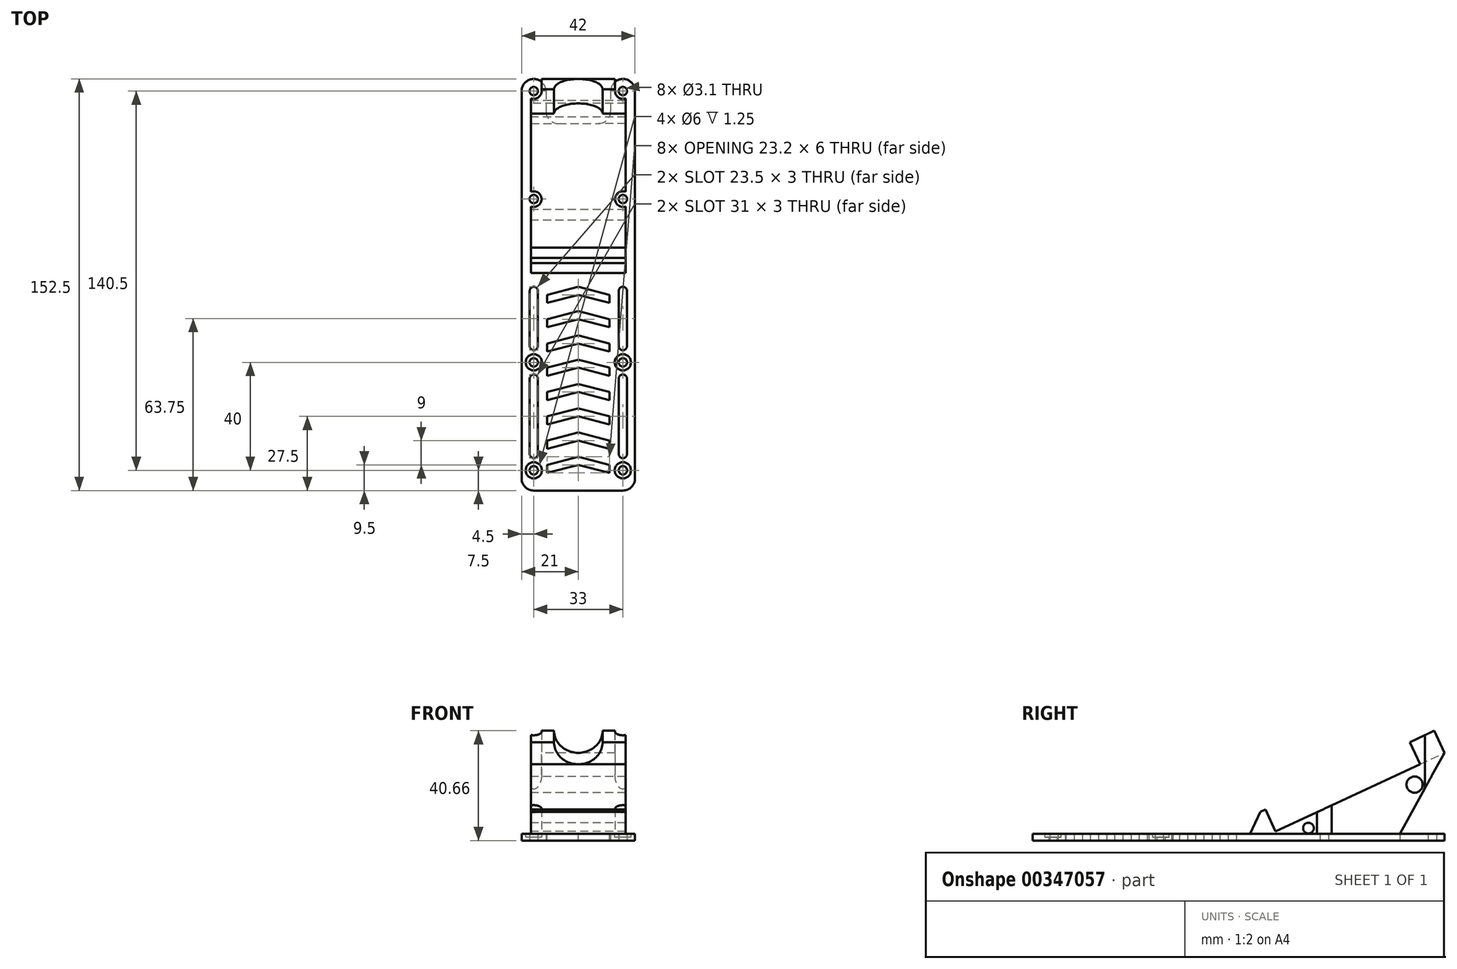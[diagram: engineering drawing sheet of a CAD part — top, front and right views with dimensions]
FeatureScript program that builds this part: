
annotation { "Feature Type Name" : "Feature", "Feature Type Description" : "" }
export const myFeature = defineFeature(function(context is Context, id is Id, definition is map)
    precondition{}
    {
        {
            var Q0;
            Q0=qCreatedBy(makeId("Top.planeOp"),FACE);
            var sketch = newSketch(context, id + "F0", { "sketchPlane" : qUnion([Q0])});
            skLineSegment(sketch, "E0.bottom", {"start": v(-16.5, 76.75) * mm, "end": v(-16.5, 76.75) * mm});
            skCircle(sketch, "E1", {"center": v(16.5, 72.25) * mm, "radius": 1.55 * mm});
            skPoint(sketch, "E2.visualSharp", {"position": v(21, 76.75) * mm});
            skArc(sketch, "E2.filletArc", {"start": v(21, 72.25) * mm, "mid": v(19.68, 75.43) * mm, "end": v(16.5, 76.75) * mm});
            skCircle(sketch, "E3", {"center": v(-16.5, 72.25) * mm, "radius": 1.55 * mm});
            skLineSegment(sketch, "E4", {"start": v(-12, 72.25) * mm, "end": v(-12, 64.75) * mm});
            skLineSegment(sketch, "E5", {"start": v(12, 72.25) * mm, "end": v(12, 64.75) * mm});
            skLineSegment(sketch, "E6", {"start": v(-7.5, 60.25) * mm, "end": v(7.5, 60.25) * mm});
            skLineSegment(sketch, "E7.trimOffspring", {"start": v(16.5, 76.75) * mm, "end": v(16.5, 76.75) * mm});
            skPoint(sketch, "E8.visualSharp", {"position": v(-12, 76.75) * mm});
            skArc(sketch, "E8.filletArc", {"start": v(-12, 72.25) * mm, "mid": v(-13.32, 75.43) * mm, "end": v(-16.5, 76.75) * mm});
            skPoint(sketch, "E9.visualSharp", {"position": v(-21, 76.75) * mm});
            skArc(sketch, "E9.filletArc", {"start": v(-16.5, 76.75) * mm, "mid": v(-19.68, 75.43) * mm, "end": v(-21, 72.25) * mm});
            skPoint(sketch, "E10.visualSharp", {"position": v(12, 76.75) * mm});
            skArc(sketch, "E10.filletArc", {"start": v(16.5, 76.75) * mm, "mid": v(13.32, 75.43) * mm, "end": v(12, 72.25) * mm});
            skArc(sketch, "E11.filletArc", {"start": v(7.5, 60.25) * mm, "mid": v(10.68, 61.57) * mm, "end": v(12, 64.75) * mm});
            skArc(sketch, "E12.filletArc", {"start": v(-12, 64.75) * mm, "mid": v(-10.68, 61.57) * mm, "end": v(-7.5, 60.25) * mm});
            skLineSegment(sketch, "E13", {"start": v(-16.5, -0.25) * mm, "end": v(-16.5, -0.25) * mm});
            skLineSegment(sketch, "E14", {"start": v(-16.5, -23.75) * mm, "end": v(-16.5, -23.75) * mm});
            skLineSegment(sketch, "E15", {"start": v(16.5, -23.75) * mm, "end": v(16.5, -23.75) * mm});
            skLineSegment(sketch, "E16", {"start": v(16.5, -0.25) * mm, "end": v(16.5, -0.25) * mm});
            skLineSegment(sketch, "E17.trimOffspring", {"start": v(15, -1.75) * mm, "end": v(15, -22.25) * mm});
            skLineSegment(sketch, "E18.trimOffspring", {"start": v(-15, -1.75) * mm, "end": v(-15, -22.25) * mm});
            skCircle(sketch, "E19", {"center": v(16.5, 32.25) * mm, "radius": 1.55 * mm});
            skCircle(sketch, "E20", {"center": v(-16.5, 32.25) * mm, "radius": 1.55 * mm});
            skPoint(sketch, "E21.visualSharp", {"position": v(18, -0.25) * mm});
            skPoint(sketch, "E22.visualSharp", {"position": v(15, -0.25) * mm});
            skArc(sketch, "E22.filletArc", {"start": v(16.5, -0.25) * mm, "mid": v(15.44, -0.69) * mm, "end": v(15, -1.75) * mm});
            skPoint(sketch, "E23.visualSharp", {"position": v(-15, -0.25) * mm});
            skArc(sketch, "E23.filletArc", {"start": v(-15, -1.75) * mm, "mid": v(-15.44, -0.69) * mm, "end": v(-16.5, -0.25) * mm});
            skPoint(sketch, "E24.visualSharp", {"position": v(-18, -0.25) * mm});
            skCircle(sketch, "E25", {"center": v(16.5, -28.25) * mm, "radius": 1.55 * mm});
            skPoint(sketch, "E25.centerSnap0", {"position": v(16.5, -23.75) * mm});
            skCircle(sketch, "E26", {"center": v(-16.5, -28.25) * mm, "radius": 1.55 * mm});
            skPoint(sketch, "E26.centerSnap0", {"position": v(-16.5, -23.75) * mm});
            skPoint(sketch, "E27.visualSharp", {"position": v(18, -23.75) * mm});
            skPoint(sketch, "E28.visualSharp", {"position": v(-15, -23.75) * mm});
            skArc(sketch, "E28.filletArc", {"start": v(-16.5, -23.75) * mm, "mid": v(-15.44, -23.31) * mm, "end": v(-15, -22.25) * mm});
            skPoint(sketch, "E29.visualSharp", {"position": v(-18, -23.75) * mm});
            skPoint(sketch, "E30.visualSharp", {"position": v(15, -23.75) * mm});
            skArc(sketch, "E30.filletArc", {"start": v(15, -22.25) * mm, "mid": v(15.44, -23.31) * mm, "end": v(16.5, -23.75) * mm});
            skPoint(sketch, "E31", {"position": v(-16.5, -68.25) * mm});
            skPoint(sketch, "E32", {"position": v(16.5, -68.25) * mm});
            skLineSegment(sketch, "E33", {"start": v(-16.5, -75.75) * mm, "end": v(16.5, -75.75) * mm});
            skLineSegment(sketch, "E34", {"start": v(-21, 72.25) * mm, "end": v(-21, -71.25) * mm});
            skLineSegment(sketch, "E35", {"start": v(21, 72.25) * mm, "end": v(21, -71.25) * mm});
            skCircle(sketch, "E36", {"center": v(-16.5, -68.25) * mm, "radius": 1.55 * mm});
            skCircle(sketch, "E37", {"center": v(16.5, -68.25) * mm, "radius": 1.55 * mm});
            skPoint(sketch, "E38.visualSharp", {"position": v(-21, -75.75) * mm});
            skArc(sketch, "E38.filletArc", {"start": v(-21, -71.25) * mm, "mid": v(-19.68, -74.43) * mm, "end": v(-16.5, -75.75) * mm});
            skPoint(sketch, "E39.visualSharp", {"position": v(21, -75.75) * mm});
            skArc(sketch, "E39.filletArc", {"start": v(16.5, -75.75) * mm, "mid": v(19.68, -74.43) * mm, "end": v(21, -71.25) * mm});
            skLineSegment(sketch, "E40", {"start": v(-15, -34.25) * mm, "end": v(-15, -62.25) * mm});
            skLineSegment(sketch, "E41", {"start": v(-16.5, -63.75) * mm, "end": v(-16.5, -63.75) * mm});
            skLineSegment(sketch, "E42", {"start": v(-16.5, -32.75) * mm, "end": v(-16.5, -32.75) * mm});
            skLineSegment(sketch, "E43", {"start": v(15, -34.25) * mm, "end": v(15, -62.25) * mm});
            skLineSegment(sketch, "E44", {"start": v(16.5, -63.75) * mm, "end": v(16.5, -63.75) * mm});
            skLineSegment(sketch, "E45", {"start": v(16.5, -32.75) * mm, "end": v(16.5, -32.75) * mm});
            skPoint(sketch, "E46.visualSharp", {"position": v(-15, -32.75) * mm});
            skArc(sketch, "E46.filletArc", {"start": v(-15, -34.25) * mm, "mid": v(-15.44, -33.19) * mm, "end": v(-16.5, -32.75) * mm});
            skPoint(sketch, "E47.visualSharp", {"position": v(15, -32.75) * mm});
            skArc(sketch, "E47.filletArc", {"start": v(16.5, -32.75) * mm, "mid": v(15.44, -33.19) * mm, "end": v(15, -34.25) * mm});
            skPoint(sketch, "E48.visualSharp", {"position": v(-15, -63.75) * mm});
            skArc(sketch, "E48.filletArc", {"start": v(-16.5, -63.75) * mm, "mid": v(-15.44, -63.31) * mm, "end": v(-15, -62.25) * mm});
            skPoint(sketch, "E49.visualSharp", {"position": v(15, -63.75) * mm});
            skArc(sketch, "E49.filletArc", {"start": v(15, -62.25) * mm, "mid": v(15.44, -63.31) * mm, "end": v(16.5, -63.75) * mm});
            skLineSegment(sketch, "E50", {"start": v(18, -1.75) * mm, "end": v(18, -22.25) * mm});
            skLineSegment(sketch, "E51", {"start": v(18, -34.25) * mm, "end": v(18, -62.25) * mm});
            skArc(sketch, "E52.filletArc", {"start": v(18, -1.75) * mm, "mid": v(17.56, -0.69) * mm, "end": v(16.5, -0.25) * mm});
            skArc(sketch, "E53.filletArc", {"start": v(16.5, -23.75) * mm, "mid": v(17.56, -23.31) * mm, "end": v(18, -22.25) * mm});
            skPoint(sketch, "E54.visualSharp", {"position": v(18, -32.75) * mm});
            skArc(sketch, "E54.filletArc", {"start": v(18, -34.25) * mm, "mid": v(17.56, -33.19) * mm, "end": v(16.5, -32.75) * mm});
            skPoint(sketch, "E55.visualSharp", {"position": v(18, -63.75) * mm});
            skArc(sketch, "E55.filletArc", {"start": v(16.5, -63.75) * mm, "mid": v(17.56, -63.31) * mm, "end": v(18, -62.25) * mm});
            skLineSegment(sketch, "E56", {"start": v(-18, -1.75) * mm, "end": v(-18, -22.25) * mm});
            skLineSegment(sketch, "E57", {"start": v(-18, -34.25) * mm, "end": v(-18, -62.25) * mm});
            skPoint(sketch, "E58.orphan", {"position": v(-21, -63.75) * mm});
            skArc(sketch, "E59.filletArc", {"start": v(-16.5, -0.25) * mm, "mid": v(-17.56, -0.69) * mm, "end": v(-18, -1.75) * mm});
            skArc(sketch, "E60.filletArc", {"start": v(-18, -22.25) * mm, "mid": v(-17.56, -23.31) * mm, "end": v(-16.5, -23.75) * mm});
            skPoint(sketch, "E61.visualSharp", {"position": v(-18, -32.75) * mm});
            skArc(sketch, "E61.filletArc", {"start": v(-16.5, -32.75) * mm, "mid": v(-17.56, -33.19) * mm, "end": v(-18, -34.25) * mm});
            skPoint(sketch, "E62.visualSharp", {"position": v(-18, -63.75) * mm});
            skArc(sketch, "E62.filletArc", {"start": v(-18, -62.25) * mm, "mid": v(-17.56, -63.31) * mm, "end": v(-16.5, -63.75) * mm});
            skSolve(sketch);
        }
        {
            var Q0;
            Q0=qCreatedBy(makeId("Right.planeOp"),FACE);
            var sketch = newSketch(context, id + "F1", { "sketchPlane" : qUnion([Q0])});
            skLineSegment(sketch, "E63", {"start": v(12.4, 2.5) * mm, "end": v(76.75, 32.5) * mm});
            skLineSegment(sketch, "E64", {"start": v(76.75, 32.5) * mm, "end": v(72.95, 40.66) * mm});
            skLineSegment(sketch, "E65", {"start": v(72.95, 40.66) * mm, "end": v(63.88, 36.44) * mm});
            skLineSegment(sketch, "E66", {"start": v(63.88, 36.44) * mm, "end": v(67.69, 28.28) * mm});
            skLineSegment(sketch, "E67", {"start": v(12.4, 2.5) * mm, "end": v(8.6, 10.66) * mm});
            skLineSegment(sketch, "E68", {"start": v(8.6, 10.66) * mm, "end": v(10.41, 11.5) * mm});
            skLineSegment(sketch, "E69", {"start": v(10.41, 11.5) * mm, "end": v(14.21, 3.35) * mm});
            skPoint(sketch, "E70.0", {"position": v(60.25, 0) * mm});
            skLineSegment(sketch, "E71", {"start": v(76.74, 0) * mm, "end": v(76.74, 2.5) * mm});
            skLineSegment(sketch, "E72", {"start": v(-5.7, 2.5) * mm, "end": v(-5.7, 0) * mm});
            skLineSegment(sketch, "E73", {"start": v(-5.7, 0) * mm, "end": v(76.74, 0) * mm});
            skLineSegment(sketch, "E74", {"start": v(-5.7, 2.5) * mm, "end": v(76.74, 2.5) * mm});
            skLineSegment(sketch, "E75", {"start": v(76.75, 32.5) * mm, "end": v(60.25, 2.5) * mm});
            skLineSegment(sketch, "E76", {"start": v(8.6, 10.66) * mm, "end": v(8.6, 2.5) * mm});
            skLineSegment(sketch, "E77", {"start": v(60.25, 2.5) * mm, "end": v(60.25, 24.81) * mm, "construction": true});
            skPoint(sketch, "E78", {"position": v(63.16, 26.17) * mm});
            skLineSegment(sketch, "E79", {"start": v(63.16, 26.17) * mm, "end": v(67.8, 16.22) * mm, "construction": true});
            skCircle(sketch, "E80", {"center": v(65.7, 20.73) * mm, "radius": 3 * mm});
            skLineSegment(sketch, "E81", {"start": v(8.6, 10.66) * mm, "end": v(4.8, 2.5) * mm});
            skCircle(sketch, "E82", {"center": v(26.37, 4.6) * mm, "radius": 2 * mm});
            skSolve(sketch);
        }
        {
            var Q0;
            {var subQ0=sQuery(id+"F1.wireOp",EDGE,"E67");Q0=makeQuery(id+"F1.imprint","IMPRINT",FACE,{"disambiguationData":[TD([[makeQuery(id+"F1.imprint","IMPRINT",EDGE,{"derivedFrom":subQ0}),-1.0]])]});}
            var Q1;
            {var subQ0=sQuery(id+"F1.wireOp",EDGE,"E64");Q1=makeQuery(id+"F1.imprint","IMPRINT",FACE,{"disambiguationData":[TD([[makeQuery(id+"F1.imprint","IMPRINT",EDGE,{"derivedFrom":subQ0}),1.0]])]});}
            var Q2;
            {var subQ4=sQuery(id+"F1.wireOp",EDGE,"E75");Q2=makeQuery(id+"F1.imprint","IMPRINT",FACE,{"disambiguationData":[TD([[makeQuery(id+"F1.imprint","IMPRINT",EDGE,{"derivedFrom":subQ4}),-1.0]])]});}
            var Q3;
            {var subQ0=sQuery(id+"F1.wireOp",EDGE,"E67");Q3=makeQuery(id+"F1.imprint","IMPRINT",FACE,{"disambiguationData":[TD([[makeQuery(id+"F1.imprint","IMPRINT",EDGE,{"derivedFrom":subQ0}),1.0]])]});}
            var Q4;
            {var subQ0=sQuery(id+"F1.wireOp",EDGE,"E76");Q4=makeQuery(id+"F1.imprint","IMPRINT",FACE,{"disambiguationData":[TD([[makeQuery(id+"F1.imprint","IMPRINT",EDGE,{"derivedFrom":subQ0}),-1.0]])]});}
            extrude(context, id + "F2", {"entities" : qUnion([Q0, Q1, Q2, Q3, Q4]), "depth" : 17.5 * mm, "hasSecondDirection" : true, "secondDirectionOppositeDirection" : true, "secondDirectionDepth" : 17.5 * mm});
        }
        {
            var Q0;
            Q0=makeQuery(id+"F2.opExtrude","SWEPT_FACE",FACE,{"disambiguationData":[OSD([sQuery(id+"F1.wireOp",EDGE,"E64")])]});
            var sketch = newSketch(context, id + "F3", { "sketchPlane" : qUnion([Q0])});
            skLineSegment(sketch, "E83.0", {"start": v(-17.5, -2.98) * mm, "end": v(17.5, -2.98) * mm, "construction": true});
            skLineSegment(sketch, "E84", {"start": v(0, -2.98) * mm, "end": v(0, 15.02) * mm, "construction": true});
            skPoint(sketch, "E84.endSnap0", {"position": v(0, -2.98) * mm});
            skCircle(sketch, "E85", {"center": v(0, 6.02) * mm, "radius": 9 * mm});
            skSolve(sketch);
        }
        {
            var Q0;
            Q0 = qSketchRegion(id + "F3", true);
            extrude(context, id + "F4", {"entities" : qUnion([Q0]), "operationType" : NewBodyOperationType.REMOVE, "oppositeDirection" : true, "depth" : 25 * mm});
        }
        {
            var Q0;
            Q0=makeQuery(id+"F0.imprint","IMPRINT",FACE,{"disambiguationData":[TD([[makeQuery(id+"F0.imprint","IMPRINT",EDGE,{"derivedFrom":sQuery(id+"F0.wireOp",EDGE,"E1")}),-1.0]])]});
            extrude(context, id + "F5", {"entities" : qUnion([Q0]), "operationType" : NewBodyOperationType.ADD, "depth" : 2.5 * mm});
        }
        {
            var Q0;
            Q0=makeQuery(id+"F5.opExtrude","CAP_FACE",FACE,{"disambiguationData":[OSD([sQuery(id+"F0.wireOp",EDGE,"E1"),sQuery(id+"F0.wireOp",EDGE,"E2.filletArc"),sQuery(id+"F0.wireOp",EDGE,"E3"),sQuery(id+"F0.wireOp",EDGE,"E4"),sQuery(id+"F0.wireOp",EDGE,"E5"),sQuery(id+"F0.wireOp",EDGE,"E6"),sQuery(id+"F0.wireOp",EDGE,"E8.filletArc"),sQuery(id+"F0.wireOp",EDGE,"E9.filletArc"),sQuery(id+"F0.wireOp",EDGE,"E10.filletArc"),sQuery(id+"F0.wireOp",EDGE,"E11.filletArc"),sQuery(id+"F0.wireOp",EDGE,"E12.filletArc"),sQuery(id+"F0.wireOp",EDGE,"E17.trimOffspring"),sQuery(id+"F0.wireOp",EDGE,"E18.trimOffspring"),sQuery(id+"F0.wireOp",EDGE,"E19"),sQuery(id+"F0.wireOp",EDGE,"E20"),sQuery(id+"F0.wireOp",EDGE,"E22.filletArc"),sQuery(id+"F0.wireOp",EDGE,"E23.filletArc"),sQuery(id+"F0.wireOp",EDGE,"E25"),sQuery(id+"F0.wireOp",EDGE,"E26"),sQuery(id+"F0.wireOp",EDGE,"E28.filletArc"),sQuery(id+"F0.wireOp",EDGE,"E30.filletArc"),sQuery(id+"F0.wireOp",EDGE,"E33"),sQuery(id+"F0.wireOp",EDGE,"E34"),sQuery(id+"F0.wireOp",EDGE,"E35"),sQuery(id+"F0.wireOp",EDGE,"E36"),sQuery(id+"F0.wireOp",EDGE,"E37"),sQuery(id+"F0.wireOp",EDGE,"E38.filletArc"),sQuery(id+"F0.wireOp",EDGE,"E39.filletArc"),sQuery(id+"F0.wireOp",EDGE,"E13"),sQuery(id+"F0.wireOp",EDGE,"E14"),sQuery(id+"F0.wireOp",EDGE,"E16"),sQuery(id+"F0.wireOp",EDGE,"E15")])],"isStart":false});
            var sketch = newSketch(context, id + "F6", { "sketchPlane" : qUnion([Q0])});
            skCircle(sketch, "E86", {"center": v(16.5, 72.25) * mm, "radius": 2.9 * mm});
            skCircle(sketch, "E87", {"center": v(-16.5, 72.25) * mm, "radius": 2.9 * mm});
            skCircle(sketch, "E88", {"center": v(-16.5, 32.25) * mm, "radius": 2.9 * mm});
            skCircle(sketch, "E89", {"center": v(16.5, 32.25) * mm, "radius": 2.9 * mm});
            skCircle(sketch, "E90", {"center": v(-16.5, -28.25) * mm, "radius": 3 * mm});
            skCircle(sketch, "E91", {"center": v(16.5, -28.25) * mm, "radius": 3 * mm});
            skCircle(sketch, "E92", {"center": v(-16.5, -68.25) * mm, "radius": 3 * mm});
            skCircle(sketch, "E93", {"center": v(16.5, -68.25) * mm, "radius": 3 * mm});
            skSolve(sketch);
        }
        {
            var Q0;
            Q0=makeQuery(id+"F6.imprint","IMPRINT",FACE,{"disambiguationData":[TD([[makeQuery(id+"F6.imprint","IMPRINT",EDGE,{"derivedFrom":makeQuery(id+"F5.opExtrude","CAP_EDGE",EDGE,{"disambiguationData":[OSD([sQuery(id+"F0.wireOp",EDGE,"E25")])],"isStart":false})}),1.0]])]});
            var Q1;
            Q1=makeQuery(id+"F6.imprint","IMPRINT",FACE,{"disambiguationData":[TD([[makeQuery(id+"F6.imprint","IMPRINT",EDGE,{"derivedFrom":makeQuery(id+"F5.opExtrude","CAP_EDGE",EDGE,{"disambiguationData":[OSD([sQuery(id+"F0.wireOp",EDGE,"E26")])],"isStart":false})}),1.0]])]});
            var Q2;
            Q2=makeQuery(id+"F6.imprint","IMPRINT",FACE,{"disambiguationData":[TD([[makeQuery(id+"F6.imprint","IMPRINT",EDGE,{"derivedFrom":makeQuery(id+"F5.opExtrude","CAP_EDGE",EDGE,{"disambiguationData":[OSD([sQuery(id+"F0.wireOp",EDGE,"E36")])],"isStart":false})}),1.0]])]});
            var Q3;
            Q3=makeQuery(id+"F6.imprint","IMPRINT",FACE,{"disambiguationData":[TD([[makeQuery(id+"F6.imprint","IMPRINT",EDGE,{"derivedFrom":makeQuery(id+"F5.opExtrude","CAP_EDGE",EDGE,{"disambiguationData":[OSD([sQuery(id+"F0.wireOp",EDGE,"E37")])],"isStart":false})}),1.0]])]});
            var Q4;
            Q4=makeQuery(id+"F6.imprint","IMPRINT",FACE,{"disambiguationData":[TD([[makeQuery(id+"F6.imprint","IMPRINT",EDGE,{"derivedFrom":sQuery(id+"F6.wireOp",EDGE,"E90")}),1.0]])]});
            var Q5;
            Q5=makeQuery(id+"F6.imprint","IMPRINT",FACE,{"disambiguationData":[TD([[makeQuery(id+"F6.imprint","IMPRINT",EDGE,{"derivedFrom":sQuery(id+"F6.wireOp",EDGE,"E91")}),1.0]])]});
            var Q6;
            Q6=makeQuery(id+"F6.imprint","IMPRINT",FACE,{"disambiguationData":[TD([[makeQuery(id+"F6.imprint","IMPRINT",EDGE,{"derivedFrom":sQuery(id+"F6.wireOp",EDGE,"E92")}),1.0]])]});
            var Q7;
            Q7=makeQuery(id+"F6.imprint","IMPRINT",FACE,{"disambiguationData":[TD([[makeQuery(id+"F6.imprint","IMPRINT",EDGE,{"derivedFrom":sQuery(id+"F6.wireOp",EDGE,"E93")}),1.0]])]});
            var Q8;
            {var subQ9=sQuery(id+"F0.wireOp",EDGE,"E20");var subQ10=makeQuery(id+"F5.opExtrude","CAP_FACE",FACE,{"disambiguationData":[OSD([sQuery(id+"F0.wireOp",EDGE,"E1"),sQuery(id+"F0.wireOp",EDGE,"E2.filletArc"),sQuery(id+"F0.wireOp",EDGE,"E3"),sQuery(id+"F0.wireOp",EDGE,"E4"),sQuery(id+"F0.wireOp",EDGE,"E5"),sQuery(id+"F0.wireOp",EDGE,"E6"),sQuery(id+"F0.wireOp",EDGE,"E8.filletArc"),sQuery(id+"F0.wireOp",EDGE,"E9.filletArc"),sQuery(id+"F0.wireOp",EDGE,"E10.filletArc"),sQuery(id+"F0.wireOp",EDGE,"E11.filletArc"),sQuery(id+"F0.wireOp",EDGE,"E12.filletArc"),sQuery(id+"F0.wireOp",EDGE,"E17.trimOffspring"),sQuery(id+"F0.wireOp",EDGE,"E18.trimOffspring"),sQuery(id+"F0.wireOp",EDGE,"E19"),subQ9,sQuery(id+"F0.wireOp",EDGE,"E22.filletArc"),sQuery(id+"F0.wireOp",EDGE,"E23.filletArc"),sQuery(id+"F0.wireOp",EDGE,"E25"),sQuery(id+"F0.wireOp",EDGE,"E26"),sQuery(id+"F0.wireOp",EDGE,"E28.filletArc"),sQuery(id+"F0.wireOp",EDGE,"E30.filletArc"),sQuery(id+"F0.wireOp",EDGE,"E33"),sQuery(id+"F0.wireOp",EDGE,"E34"),sQuery(id+"F0.wireOp",EDGE,"E35"),sQuery(id+"F0.wireOp",EDGE,"E36"),sQuery(id+"F0.wireOp",EDGE,"E37"),sQuery(id+"F0.wireOp",EDGE,"E38.filletArc"),sQuery(id+"F0.wireOp",EDGE,"E39.filletArc"),sQuery(id+"F0.wireOp",EDGE,"E13"),sQuery(id+"F0.wireOp",EDGE,"E14"),sQuery(id+"F0.wireOp",EDGE,"E16"),sQuery(id+"F0.wireOp",EDGE,"E15"),sQuery(id+"F0.wireOp",EDGE,"E40"),sQuery(id+"F0.wireOp",EDGE,"E41"),sQuery(id+"F0.wireOp",EDGE,"E42"),sQuery(id+"F0.wireOp",EDGE,"E43"),sQuery(id+"F0.wireOp",EDGE,"E44"),sQuery(id+"F0.wireOp",EDGE,"E45"),sQuery(id+"F0.wireOp",EDGE,"E46.filletArc"),sQuery(id+"F0.wireOp",EDGE,"E47.filletArc"),sQuery(id+"F0.wireOp",EDGE,"E48.filletArc"),sQuery(id+"F0.wireOp",EDGE,"E49.filletArc")])],"isStart":false});var subQ17=makeQuery(id+"F5.boolean.opBoolean","SPLIT",EDGE,{"disambiguationData":[topologyDisambiguationEdgeConnected([subQ10])],"derivedFrom":makeQuery(id+"F5.opExtrude","CAP_EDGE",EDGE,{"disambiguationData":[OSD([subQ9])],"isStart":false})});Q8=makeQuery(id+"F6.imprint","IMPRINT",FACE,{"disambiguationData":[TD([[makeQuery(id+"F6.imprint","IMPRINT",EDGE,{"derivedFrom":subQ17}),1.0]])]});}
            var Q9;
            {var subQ9=sQuery(id+"F0.wireOp",EDGE,"E19");var subQ10=makeQuery(id+"F5.opExtrude","CAP_FACE",FACE,{"disambiguationData":[OSD([sQuery(id+"F0.wireOp",EDGE,"E1"),sQuery(id+"F0.wireOp",EDGE,"E2.filletArc"),sQuery(id+"F0.wireOp",EDGE,"E3"),sQuery(id+"F0.wireOp",EDGE,"E4"),sQuery(id+"F0.wireOp",EDGE,"E5"),sQuery(id+"F0.wireOp",EDGE,"E6"),sQuery(id+"F0.wireOp",EDGE,"E8.filletArc"),sQuery(id+"F0.wireOp",EDGE,"E9.filletArc"),sQuery(id+"F0.wireOp",EDGE,"E10.filletArc"),sQuery(id+"F0.wireOp",EDGE,"E11.filletArc"),sQuery(id+"F0.wireOp",EDGE,"E12.filletArc"),sQuery(id+"F0.wireOp",EDGE,"E17.trimOffspring"),sQuery(id+"F0.wireOp",EDGE,"E18.trimOffspring"),subQ9,sQuery(id+"F0.wireOp",EDGE,"E20"),sQuery(id+"F0.wireOp",EDGE,"E22.filletArc"),sQuery(id+"F0.wireOp",EDGE,"E23.filletArc"),sQuery(id+"F0.wireOp",EDGE,"E25"),sQuery(id+"F0.wireOp",EDGE,"E26"),sQuery(id+"F0.wireOp",EDGE,"E28.filletArc"),sQuery(id+"F0.wireOp",EDGE,"E30.filletArc"),sQuery(id+"F0.wireOp",EDGE,"E33"),sQuery(id+"F0.wireOp",EDGE,"E34"),sQuery(id+"F0.wireOp",EDGE,"E35"),sQuery(id+"F0.wireOp",EDGE,"E36"),sQuery(id+"F0.wireOp",EDGE,"E37"),sQuery(id+"F0.wireOp",EDGE,"E38.filletArc"),sQuery(id+"F0.wireOp",EDGE,"E39.filletArc"),sQuery(id+"F0.wireOp",EDGE,"E13"),sQuery(id+"F0.wireOp",EDGE,"E14"),sQuery(id+"F0.wireOp",EDGE,"E16"),sQuery(id+"F0.wireOp",EDGE,"E15"),sQuery(id+"F0.wireOp",EDGE,"E40"),sQuery(id+"F0.wireOp",EDGE,"E41"),sQuery(id+"F0.wireOp",EDGE,"E42"),sQuery(id+"F0.wireOp",EDGE,"E43"),sQuery(id+"F0.wireOp",EDGE,"E44"),sQuery(id+"F0.wireOp",EDGE,"E45"),sQuery(id+"F0.wireOp",EDGE,"E46.filletArc"),sQuery(id+"F0.wireOp",EDGE,"E47.filletArc"),sQuery(id+"F0.wireOp",EDGE,"E48.filletArc"),sQuery(id+"F0.wireOp",EDGE,"E49.filletArc")])],"isStart":false});var subQ17=makeQuery(id+"F5.boolean.opBoolean","SPLIT",EDGE,{"disambiguationData":[topologyDisambiguationEdgeConnected([subQ10])],"derivedFrom":makeQuery(id+"F5.opExtrude","CAP_EDGE",EDGE,{"disambiguationData":[OSD([subQ9])],"isStart":false})});Q9=makeQuery(id+"F6.imprint","IMPRINT",FACE,{"disambiguationData":[TD([[makeQuery(id+"F6.imprint","IMPRINT",EDGE,{"derivedFrom":subQ17}),1.0]])]});}
            var Q10;
            {var subQ9=sQuery(id+"F0.wireOp",EDGE,"E20");var subQ10=makeQuery(id+"F5.opExtrude","CAP_FACE",FACE,{"disambiguationData":[OSD([sQuery(id+"F0.wireOp",EDGE,"E1"),sQuery(id+"F0.wireOp",EDGE,"E2.filletArc"),sQuery(id+"F0.wireOp",EDGE,"E3"),sQuery(id+"F0.wireOp",EDGE,"E4"),sQuery(id+"F0.wireOp",EDGE,"E5"),sQuery(id+"F0.wireOp",EDGE,"E6"),sQuery(id+"F0.wireOp",EDGE,"E8.filletArc"),sQuery(id+"F0.wireOp",EDGE,"E9.filletArc"),sQuery(id+"F0.wireOp",EDGE,"E10.filletArc"),sQuery(id+"F0.wireOp",EDGE,"E11.filletArc"),sQuery(id+"F0.wireOp",EDGE,"E12.filletArc"),sQuery(id+"F0.wireOp",EDGE,"E17.trimOffspring"),sQuery(id+"F0.wireOp",EDGE,"E18.trimOffspring"),sQuery(id+"F0.wireOp",EDGE,"E19"),subQ9,sQuery(id+"F0.wireOp",EDGE,"E22.filletArc"),sQuery(id+"F0.wireOp",EDGE,"E23.filletArc"),sQuery(id+"F0.wireOp",EDGE,"E25"),sQuery(id+"F0.wireOp",EDGE,"E26"),sQuery(id+"F0.wireOp",EDGE,"E28.filletArc"),sQuery(id+"F0.wireOp",EDGE,"E30.filletArc"),sQuery(id+"F0.wireOp",EDGE,"E33"),sQuery(id+"F0.wireOp",EDGE,"E34"),sQuery(id+"F0.wireOp",EDGE,"E35"),sQuery(id+"F0.wireOp",EDGE,"E36"),sQuery(id+"F0.wireOp",EDGE,"E37"),sQuery(id+"F0.wireOp",EDGE,"E38.filletArc"),sQuery(id+"F0.wireOp",EDGE,"E39.filletArc"),sQuery(id+"F0.wireOp",EDGE,"E13"),sQuery(id+"F0.wireOp",EDGE,"E14"),sQuery(id+"F0.wireOp",EDGE,"E16"),sQuery(id+"F0.wireOp",EDGE,"E15"),sQuery(id+"F0.wireOp",EDGE,"E40"),sQuery(id+"F0.wireOp",EDGE,"E41"),sQuery(id+"F0.wireOp",EDGE,"E42"),sQuery(id+"F0.wireOp",EDGE,"E43"),sQuery(id+"F0.wireOp",EDGE,"E44"),sQuery(id+"F0.wireOp",EDGE,"E45"),sQuery(id+"F0.wireOp",EDGE,"E46.filletArc"),sQuery(id+"F0.wireOp",EDGE,"E47.filletArc"),sQuery(id+"F0.wireOp",EDGE,"E48.filletArc"),sQuery(id+"F0.wireOp",EDGE,"E49.filletArc")])],"isStart":false});var subQ17=makeQuery(id+"F5.boolean.opBoolean","SPLIT",EDGE,{"disambiguationData":[topologyDisambiguationEdgeConnected([subQ10])],"derivedFrom":makeQuery(id+"F5.opExtrude","CAP_EDGE",EDGE,{"disambiguationData":[OSD([subQ9])],"isStart":false})});Q10=makeQuery(id+"F6.imprint","IMPRINT",FACE,{"disambiguationData":[TD([[makeQuery(id+"F6.imprint","IMPRINT",EDGE,{"derivedFrom":subQ17}),-1.0]])]});}
            var Q11;
            {var subQ9=sQuery(id+"F0.wireOp",EDGE,"E19");var subQ10=makeQuery(id+"F5.opExtrude","CAP_FACE",FACE,{"disambiguationData":[OSD([sQuery(id+"F0.wireOp",EDGE,"E1"),sQuery(id+"F0.wireOp",EDGE,"E2.filletArc"),sQuery(id+"F0.wireOp",EDGE,"E3"),sQuery(id+"F0.wireOp",EDGE,"E4"),sQuery(id+"F0.wireOp",EDGE,"E5"),sQuery(id+"F0.wireOp",EDGE,"E6"),sQuery(id+"F0.wireOp",EDGE,"E8.filletArc"),sQuery(id+"F0.wireOp",EDGE,"E9.filletArc"),sQuery(id+"F0.wireOp",EDGE,"E10.filletArc"),sQuery(id+"F0.wireOp",EDGE,"E11.filletArc"),sQuery(id+"F0.wireOp",EDGE,"E12.filletArc"),sQuery(id+"F0.wireOp",EDGE,"E17.trimOffspring"),sQuery(id+"F0.wireOp",EDGE,"E18.trimOffspring"),subQ9,sQuery(id+"F0.wireOp",EDGE,"E20"),sQuery(id+"F0.wireOp",EDGE,"E22.filletArc"),sQuery(id+"F0.wireOp",EDGE,"E23.filletArc"),sQuery(id+"F0.wireOp",EDGE,"E25"),sQuery(id+"F0.wireOp",EDGE,"E26"),sQuery(id+"F0.wireOp",EDGE,"E28.filletArc"),sQuery(id+"F0.wireOp",EDGE,"E30.filletArc"),sQuery(id+"F0.wireOp",EDGE,"E33"),sQuery(id+"F0.wireOp",EDGE,"E34"),sQuery(id+"F0.wireOp",EDGE,"E35"),sQuery(id+"F0.wireOp",EDGE,"E36"),sQuery(id+"F0.wireOp",EDGE,"E37"),sQuery(id+"F0.wireOp",EDGE,"E38.filletArc"),sQuery(id+"F0.wireOp",EDGE,"E39.filletArc"),sQuery(id+"F0.wireOp",EDGE,"E13"),sQuery(id+"F0.wireOp",EDGE,"E14"),sQuery(id+"F0.wireOp",EDGE,"E16"),sQuery(id+"F0.wireOp",EDGE,"E15"),sQuery(id+"F0.wireOp",EDGE,"E40"),sQuery(id+"F0.wireOp",EDGE,"E41"),sQuery(id+"F0.wireOp",EDGE,"E42"),sQuery(id+"F0.wireOp",EDGE,"E43"),sQuery(id+"F0.wireOp",EDGE,"E44"),sQuery(id+"F0.wireOp",EDGE,"E45"),sQuery(id+"F0.wireOp",EDGE,"E46.filletArc"),sQuery(id+"F0.wireOp",EDGE,"E47.filletArc"),sQuery(id+"F0.wireOp",EDGE,"E48.filletArc"),sQuery(id+"F0.wireOp",EDGE,"E49.filletArc")])],"isStart":false});var subQ17=makeQuery(id+"F5.boolean.opBoolean","SPLIT",EDGE,{"disambiguationData":[topologyDisambiguationEdgeConnected([subQ10])],"derivedFrom":makeQuery(id+"F5.opExtrude","CAP_EDGE",EDGE,{"disambiguationData":[OSD([subQ9])],"isStart":false})});Q11=makeQuery(id+"F6.imprint","IMPRINT",FACE,{"disambiguationData":[TD([[makeQuery(id+"F6.imprint","IMPRINT",EDGE,{"derivedFrom":subQ17}),-1.0]])]});}
            var Q12;
            Q12=makeQuery(id+"F6.imprint","IMPRINT",FACE,{"disambiguationData":[TD([[makeQuery(id+"F6.imprint","IMPRINT",EDGE,{"derivedFrom":sQuery(id+"F6.wireOp",EDGE,"E86")}),1.0]])]});
            var Q13;
            Q13=makeQuery(id+"F6.imprint","IMPRINT",FACE,{"disambiguationData":[TD([[makeQuery(id+"F6.imprint","IMPRINT",EDGE,{"derivedFrom":makeQuery(id+"F5.opExtrude","CAP_EDGE",EDGE,{"disambiguationData":[OSD([sQuery(id+"F0.wireOp",EDGE,"E1")])],"isStart":false})}),1.0]])]});
            var Q14;
            Q14=makeQuery(id+"F6.imprint","IMPRINT",FACE,{"disambiguationData":[TD([[makeQuery(id+"F6.imprint","IMPRINT",EDGE,{"derivedFrom":sQuery(id+"F6.wireOp",EDGE,"E87")}),1.0]])]});
            var Q15;
            Q15=makeQuery(id+"F6.imprint","IMPRINT",FACE,{"disambiguationData":[TD([[makeQuery(id+"F6.imprint","IMPRINT",EDGE,{"derivedFrom":makeQuery(id+"F5.opExtrude","CAP_EDGE",EDGE,{"disambiguationData":[OSD([sQuery(id+"F0.wireOp",EDGE,"E3")])],"isStart":false})}),1.0]])]});
            extrude(context, id + "F7", {"entities" : qUnion([Q0, Q1, Q2, Q3, Q4, Q5, Q6, Q7, Q8, Q9, Q10, Q11, Q12, Q13, Q14, Q15]), "operationType" : NewBodyOperationType.REMOVE, "depth" : 50 * mm});
        }
        {
            var Q0;
            Q0=makeQuery(id+"F5.opExtrude","CAP_FACE",FACE,{"disambiguationData":[OSD([sQuery(id+"F0.wireOp",EDGE,"E1"),sQuery(id+"F0.wireOp",EDGE,"E2.filletArc"),sQuery(id+"F0.wireOp",EDGE,"E3"),sQuery(id+"F0.wireOp",EDGE,"E4"),sQuery(id+"F0.wireOp",EDGE,"E5"),sQuery(id+"F0.wireOp",EDGE,"E6"),sQuery(id+"F0.wireOp",EDGE,"E8.filletArc"),sQuery(id+"F0.wireOp",EDGE,"E9.filletArc"),sQuery(id+"F0.wireOp",EDGE,"E10.filletArc"),sQuery(id+"F0.wireOp",EDGE,"E11.filletArc"),sQuery(id+"F0.wireOp",EDGE,"E12.filletArc"),sQuery(id+"F0.wireOp",EDGE,"E17.trimOffspring"),sQuery(id+"F0.wireOp",EDGE,"E18.trimOffspring"),sQuery(id+"F0.wireOp",EDGE,"E19"),sQuery(id+"F0.wireOp",EDGE,"E20"),sQuery(id+"F0.wireOp",EDGE,"E22.filletArc"),sQuery(id+"F0.wireOp",EDGE,"E23.filletArc"),sQuery(id+"F0.wireOp",EDGE,"E25"),sQuery(id+"F0.wireOp",EDGE,"E26"),sQuery(id+"F0.wireOp",EDGE,"E28.filletArc"),sQuery(id+"F0.wireOp",EDGE,"E30.filletArc"),sQuery(id+"F0.wireOp",EDGE,"E33"),sQuery(id+"F0.wireOp",EDGE,"E34"),sQuery(id+"F0.wireOp",EDGE,"E35"),sQuery(id+"F0.wireOp",EDGE,"E36"),sQuery(id+"F0.wireOp",EDGE,"E37"),sQuery(id+"F0.wireOp",EDGE,"E38.filletArc"),sQuery(id+"F0.wireOp",EDGE,"E39.filletArc"),sQuery(id+"F0.wireOp",EDGE,"E13"),sQuery(id+"F0.wireOp",EDGE,"E14"),sQuery(id+"F0.wireOp",EDGE,"E16"),sQuery(id+"F0.wireOp",EDGE,"E15"),sQuery(id+"F0.wireOp",EDGE,"E40"),sQuery(id+"F0.wireOp",EDGE,"E41"),sQuery(id+"F0.wireOp",EDGE,"E42"),sQuery(id+"F0.wireOp",EDGE,"E43"),sQuery(id+"F0.wireOp",EDGE,"E44"),sQuery(id+"F0.wireOp",EDGE,"E45"),sQuery(id+"F0.wireOp",EDGE,"E46.filletArc"),sQuery(id+"F0.wireOp",EDGE,"E47.filletArc"),sQuery(id+"F0.wireOp",EDGE,"E48.filletArc"),sQuery(id+"F0.wireOp",EDGE,"E49.filletArc")])],"isStart":false});
            var sketch = newSketch(context, id + "F8", { "sketchPlane" : qUnion([Q0])});
            skLineSegment(sketch, "E94", {"start": v(-11.6, -0.25) * mm, "end": v(-11.6, -75.75) * mm, "construction": true});
            skLineSegment(sketch, "E95", {"start": v(11.6, -0.25) * mm, "end": v(11.6, -75.75) * mm, "construction": true});
            skPoint(sketch, "E96", {"position": v(0, -0.25) * mm});
            skPoint(sketch, "E97", {"position": v(-11.6, -3.25) * mm});
            skPoint(sketch, "E98", {"position": v(-11.6, -6.25) * mm});
            skLineSegment(sketch, "E99", {"start": v(0, -0.25) * mm, "end": v(-11.6, -3.25) * mm});
            skLineSegment(sketch, "E100", {"start": v(-11.6, -3.25) * mm, "end": v(-11.6, -6.25) * mm});
            skLineSegment(sketch, "E101", {"start": v(-11.6, -6.25) * mm, "end": v(0, -3.25) * mm});
            skLineSegment(sketch, "E102", {"start": v(0, -3.25) * mm, "end": v(11.6, -6.25) * mm});
            skLineSegment(sketch, "E103", {"start": v(11.6, -6.25) * mm, "end": v(11.6, -3.25) * mm});
            skLineSegment(sketch, "E104", {"start": v(11.6, -3.25) * mm, "end": v(0, -0.25) * mm});
            skPoint(sketch, "E105", {"position": v(-11.6, -24.25) * mm});
            skLineSegment(sketch, "E106.1.0.0", {"start": v(-11.6, -12.25) * mm, "end": v(-11.6, -15.25) * mm});
            skLineSegment(sketch, "E106.1.0.1", {"start": v(-11.6, -15.25) * mm, "end": v(0, -12.25) * mm});
            skLineSegment(sketch, "E106.1.0.2", {"start": v(11.6, -15.25) * mm, "end": v(11.6, -12.25) * mm});
            skPoint(sketch, "E106.1.0.3", {"position": v(-11.6, -15.25) * mm});
            skLineSegment(sketch, "E106.1.0.4", {"start": v(0, -12.25) * mm, "end": v(11.6, -15.25) * mm});
            skLineSegment(sketch, "E106.1.0.5", {"start": v(11.6, -12.25) * mm, "end": v(0, -9.25) * mm});
            skLineSegment(sketch, "E106.1.0.6", {"start": v(0, -9.25) * mm, "end": v(-11.6, -12.25) * mm});
            skPoint(sketch, "E106.1.0.7", {"position": v(0, -9.25) * mm});
            skPoint(sketch, "E106.1.0.8", {"position": v(-11.6, -12.25) * mm});
            skLineSegment(sketch, "E106.2.0.0", {"start": v(-11.6, -21.25) * mm, "end": v(-11.6, -24.25) * mm});
            skLineSegment(sketch, "E106.2.0.1", {"start": v(-11.6, -24.25) * mm, "end": v(0, -21.25) * mm});
            skLineSegment(sketch, "E106.2.0.2", {"start": v(11.6, -24.25) * mm, "end": v(11.6, -21.25) * mm});
            skLineSegment(sketch, "E106.2.0.4", {"start": v(0, -21.25) * mm, "end": v(11.6, -24.25) * mm});
            skLineSegment(sketch, "E106.2.0.5", {"start": v(11.6, -21.25) * mm, "end": v(0, -18.25) * mm});
            skLineSegment(sketch, "E106.2.0.6", {"start": v(0, -18.25) * mm, "end": v(-11.6, -21.25) * mm});
            skPoint(sketch, "E106.2.0.7", {"position": v(0, -18.25) * mm});
            skPoint(sketch, "E106.2.0.8", {"position": v(-11.6, -21.25) * mm});
            skLineSegment(sketch, "E106.3.0.0", {"start": v(-11.6, -30.25) * mm, "end": v(-11.6, -33.25) * mm});
            skLineSegment(sketch, "E106.3.0.1", {"start": v(-11.6, -33.25) * mm, "end": v(0, -30.25) * mm});
            skLineSegment(sketch, "E106.3.0.2", {"start": v(11.6, -33.25) * mm, "end": v(11.6, -30.25) * mm});
            skPoint(sketch, "E106.3.0.3", {"position": v(-11.6, -33.25) * mm});
            skLineSegment(sketch, "E106.3.0.4", {"start": v(0, -30.25) * mm, "end": v(11.6, -33.25) * mm});
            skLineSegment(sketch, "E106.3.0.5", {"start": v(11.6, -30.25) * mm, "end": v(0, -27.25) * mm});
            skLineSegment(sketch, "E106.3.0.6", {"start": v(0, -27.25) * mm, "end": v(-11.6, -30.25) * mm});
            skPoint(sketch, "E106.3.0.7", {"position": v(0, -27.25) * mm});
            skPoint(sketch, "E106.3.0.8", {"position": v(-11.6, -30.25) * mm});
            skLineSegment(sketch, "E106.4.0.0", {"start": v(-11.6, -39.25) * mm, "end": v(-11.6, -42.25) * mm});
            skLineSegment(sketch, "E106.4.0.1", {"start": v(-11.6, -42.25) * mm, "end": v(0, -39.25) * mm});
            skLineSegment(sketch, "E106.4.0.2", {"start": v(11.6, -42.25) * mm, "end": v(11.6, -39.25) * mm});
            skPoint(sketch, "E106.4.0.3", {"position": v(-11.6, -42.25) * mm});
            skLineSegment(sketch, "E106.4.0.4", {"start": v(0, -39.25) * mm, "end": v(11.6, -42.25) * mm});
            skLineSegment(sketch, "E106.4.0.5", {"start": v(11.6, -39.25) * mm, "end": v(0, -36.25) * mm});
            skLineSegment(sketch, "E106.4.0.6", {"start": v(0, -36.25) * mm, "end": v(-11.6, -39.25) * mm});
            skPoint(sketch, "E106.4.0.7", {"position": v(0, -36.25) * mm});
            skPoint(sketch, "E106.4.0.8", {"position": v(-11.6, -39.25) * mm});
            skLineSegment(sketch, "E106.5.0.0", {"start": v(-11.6, -48.25) * mm, "end": v(-11.6, -51.25) * mm});
            skLineSegment(sketch, "E106.5.0.1", {"start": v(-11.6, -51.25) * mm, "end": v(0, -48.25) * mm});
            skLineSegment(sketch, "E106.5.0.2", {"start": v(11.6, -51.25) * mm, "end": v(11.6, -48.25) * mm});
            skPoint(sketch, "E106.5.0.3", {"position": v(-11.6, -51.25) * mm});
            skLineSegment(sketch, "E106.5.0.4", {"start": v(0, -48.25) * mm, "end": v(11.6, -51.25) * mm});
            skLineSegment(sketch, "E106.5.0.5", {"start": v(11.6, -48.25) * mm, "end": v(0, -45.25) * mm});
            skLineSegment(sketch, "E106.5.0.6", {"start": v(0, -45.25) * mm, "end": v(-11.6, -48.25) * mm});
            skPoint(sketch, "E106.5.0.7", {"position": v(0, -45.25) * mm});
            skPoint(sketch, "E106.5.0.8", {"position": v(-11.6, -48.25) * mm});
            skLineSegment(sketch, "E106.6.0.0", {"start": v(-11.6, -57.25) * mm, "end": v(-11.6, -60.25) * mm});
            skLineSegment(sketch, "E106.6.0.1", {"start": v(-11.6, -60.25) * mm, "end": v(0, -57.25) * mm});
            skLineSegment(sketch, "E106.6.0.2", {"start": v(11.6, -60.25) * mm, "end": v(11.6, -57.25) * mm});
            skPoint(sketch, "E106.6.0.3", {"position": v(-11.6, -60.25) * mm});
            skLineSegment(sketch, "E106.6.0.4", {"start": v(0, -57.25) * mm, "end": v(11.6, -60.25) * mm});
            skLineSegment(sketch, "E106.6.0.5", {"start": v(11.6, -57.25) * mm, "end": v(0, -54.25) * mm});
            skLineSegment(sketch, "E106.6.0.6", {"start": v(0, -54.25) * mm, "end": v(-11.6, -57.25) * mm});
            skPoint(sketch, "E106.6.0.7", {"position": v(0, -54.25) * mm});
            skPoint(sketch, "E106.6.0.8", {"position": v(-11.6, -57.25) * mm});
            skLineSegment(sketch, "E106.7.0.0", {"start": v(-11.6, -66.25) * mm, "end": v(-11.6, -69.25) * mm});
            skLineSegment(sketch, "E106.7.0.1", {"start": v(-11.6, -69.25) * mm, "end": v(0, -66.25) * mm});
            skLineSegment(sketch, "E106.7.0.2", {"start": v(11.6, -69.25) * mm, "end": v(11.6, -66.25) * mm});
            skPoint(sketch, "E106.7.0.3", {"position": v(-11.6, -69.25) * mm});
            skLineSegment(sketch, "E106.7.0.4", {"start": v(0, -66.25) * mm, "end": v(11.6, -69.25) * mm});
            skLineSegment(sketch, "E106.7.0.5", {"start": v(11.6, -66.25) * mm, "end": v(0, -63.25) * mm});
            skLineSegment(sketch, "E106.7.0.6", {"start": v(0, -63.25) * mm, "end": v(-11.6, -66.25) * mm});
            skPoint(sketch, "E106.7.0.7", {"position": v(0, -63.25) * mm});
            skPoint(sketch, "E106.7.0.8", {"position": v(-11.6, -66.25) * mm});
            skLineSegment(sketch, "E106.direction1", {"start": v(-11.6, -6.25) * mm, "end": v(-11.6, -15.25) * mm, "construction": true});
            skLineSegment(sketch, "E107", {"start": v(-16.5, -0.25) * mm, "end": v(16.5, -0.25) * mm, "construction": true});
            skSolve(sketch);
        }
        {
            var Q0;
            Q0 = qSketchRegion(id + "F8", true);
            extrude(context, id + "F9", {"entities" : qUnion([Q0]), "operationType" : NewBodyOperationType.REMOVE, "oppositeDirection" : true, "depth" : 25 * mm});
        }
        {
            var Q0;
            Q0=makeQuery(id+"F7.boolean.opBoolean","MERGE",FACE,{"derivedFrom":[makeQuery(id+"F5.opExtrude","CAP_FACE",FACE,{"disambiguationData":[OSD([sQuery(id+"F0.wireOp",EDGE,"E1"),sQuery(id+"F0.wireOp",EDGE,"E2.filletArc"),sQuery(id+"F0.wireOp",EDGE,"E3"),sQuery(id+"F0.wireOp",EDGE,"E4"),sQuery(id+"F0.wireOp",EDGE,"E5"),sQuery(id+"F0.wireOp",EDGE,"E6"),sQuery(id+"F0.wireOp",EDGE,"E8.filletArc"),sQuery(id+"F0.wireOp",EDGE,"E9.filletArc"),sQuery(id+"F0.wireOp",EDGE,"E10.filletArc"),sQuery(id+"F0.wireOp",EDGE,"E11.filletArc"),sQuery(id+"F0.wireOp",EDGE,"E12.filletArc"),sQuery(id+"F0.wireOp",EDGE,"E17.trimOffspring"),sQuery(id+"F0.wireOp",EDGE,"E18.trimOffspring"),sQuery(id+"F0.wireOp",EDGE,"E19"),sQuery(id+"F0.wireOp",EDGE,"E20"),sQuery(id+"F0.wireOp",EDGE,"E22.filletArc"),sQuery(id+"F0.wireOp",EDGE,"E23.filletArc"),sQuery(id+"F0.wireOp",EDGE,"E25"),sQuery(id+"F0.wireOp",EDGE,"E26"),sQuery(id+"F0.wireOp",EDGE,"E28.filletArc"),sQuery(id+"F0.wireOp",EDGE,"E30.filletArc"),sQuery(id+"F0.wireOp",EDGE,"E33"),sQuery(id+"F0.wireOp",EDGE,"E34"),sQuery(id+"F0.wireOp",EDGE,"E35"),sQuery(id+"F0.wireOp",EDGE,"E36"),sQuery(id+"F0.wireOp",EDGE,"E37"),sQuery(id+"F0.wireOp",EDGE,"E38.filletArc"),sQuery(id+"F0.wireOp",EDGE,"E39.filletArc"),sQuery(id+"F0.wireOp",EDGE,"E13"),sQuery(id+"F0.wireOp",EDGE,"E14"),sQuery(id+"F0.wireOp",EDGE,"E16"),sQuery(id+"F0.wireOp",EDGE,"E15"),sQuery(id+"F0.wireOp",EDGE,"E40"),sQuery(id+"F0.wireOp",EDGE,"E41"),sQuery(id+"F0.wireOp",EDGE,"E42"),sQuery(id+"F0.wireOp",EDGE,"E43"),sQuery(id+"F0.wireOp",EDGE,"E44"),sQuery(id+"F0.wireOp",EDGE,"E45"),sQuery(id+"F0.wireOp",EDGE,"E46.filletArc"),sQuery(id+"F0.wireOp",EDGE,"E47.filletArc"),sQuery(id+"F0.wireOp",EDGE,"E48.filletArc"),sQuery(id+"F0.wireOp",EDGE,"E49.filletArc")])],"isStart":false}),makeQuery(id+"F7.opExtrude","CAP_FACE",FACE,{"disambiguationData":[OSD([sQuery(id+"F6.wireOp",EDGE,"E88")])],"isStart":true}),makeQuery(id+"F7.opExtrude","CAP_FACE",FACE,{"disambiguationData":[OSD([sQuery(id+"F6.wireOp",EDGE,"E89")])],"isStart":true})]});
            var sketch = newSketch(context, id + "F10", { "sketchPlane" : qUnion([Q0])});
            skCircle(sketch, "E108.0", {"center": v(16.5, 72.25) * mm, "radius": 2.9 * mm, "construction": true});
            skCircle(sketch, "E109.0", {"center": v(-16.5, 72.25) * mm, "radius": 2.9 * mm, "construction": true});
            skArc(sketch, "E110.1", {"start": v(16.5, 76.75) * mm, "mid": v(13.32, 75.43) * mm, "end": v(12, 72.25) * mm, "construction": true});
            skLineSegment(sketch, "E110.2", {"start": v(13.68, 72.95) * mm, "end": v(9, 72.95) * mm, "construction": true});
            skArc(sketch, "E110.3.0", {"start": v(13.68, 72.95) * mm, "mid": v(14.56, 70.1) * mm, "end": v(17.5, 69.53) * mm, "construction": true});
            skLineSegment(sketch, "E110.3.1", {"start": v(13.68, 72.95) * mm, "end": v(9, 72.95) * mm, "construction": true});
            skLineSegment(sketch, "E110.3.2", {"start": v(9, 72.95) * mm, "end": v(9, 64.27) * mm, "construction": true});
            skLineSegment(sketch, "E110.3.3", {"start": v(9, 64.27) * mm, "end": v(17.5, 64.27) * mm, "construction": true});
            skLineSegment(sketch, "E110.3.4", {"start": v(17.5, 64.27) * mm, "end": v(17.5, 69.53) * mm, "construction": true});
            skArc(sketch, "E111.0.0", {"start": v(-13.68, 72.95) * mm, "mid": v(-15.14, 74.81) * mm, "end": v(-17.5, 74.97) * mm, "construction": true});
            skLineSegment(sketch, "E111.0.1", {"start": v(-13.68, 72.95) * mm, "end": v(-9, 72.95) * mm, "construction": true});
            skEllipticalArc(sketch, "E111.0.2", {"construction": true});
            skLineSegment(sketch, "E111.0.3", {"start": v(0, 76.75) * mm, "end": v(-17.5, 76.75) * mm, "construction": true});
            skLineSegment(sketch, "E111.0.4", {"start": v(-17.5, 76.75) * mm, "end": v(-17.5, 74.97) * mm, "construction": true});
            skArc(sketch, "E111.1.0", {"start": v(-17.5, 69.53) * mm, "mid": v(-14.56, 70.1) * mm, "end": v(-13.68, 72.95) * mm, "construction": true});
            skLineSegment(sketch, "E111.1.1", {"start": v(-17.5, 69.53) * mm, "end": v(-17.5, 64.27) * mm, "construction": true});
            skLineSegment(sketch, "E111.1.2", {"start": v(-17.5, 64.27) * mm, "end": v(-9, 64.27) * mm, "construction": true});
            skLineSegment(sketch, "E111.1.3", {"start": v(-9, 64.27) * mm, "end": v(-9, 72.95) * mm, "construction": true});
            skLineSegment(sketch, "E111.1.4", {"start": v(-9, 72.95) * mm, "end": v(-13.68, 72.95) * mm, "construction": true});
            skLineSegment(sketch, "E112", {"start": v(16.5, 72.25) * mm, "end": v(17.5, 74.97) * mm});
            skLineSegment(sketch, "E113", {"start": v(17.5, 76.75) * mm, "end": v(17.5, 74.97) * mm});
            skLineSegment(sketch, "E114", {"start": v(13.6, 76.75) * mm, "end": v(17.5, 76.75) * mm});
            skLineSegment(sketch, "E115", {"start": v(-16.5, 72.25) * mm, "end": v(-17.5, 74.97) * mm});
            skLineSegment(sketch, "E116", {"start": v(-17.5, 76.75) * mm, "end": v(-17.5, 74.97) * mm});
            skLineSegment(sketch, "E117", {"start": v(-16.5, 72.25) * mm, "end": v(-13.6, 72.25) * mm});
            skLineSegment(sketch, "E118", {"start": v(-13.6, 72.25) * mm, "end": v(-13.6, 76.75) * mm});
            skLineSegment(sketch, "E119", {"start": v(-13.6, 76.75) * mm, "end": v(-17.5, 76.75) * mm});
            skLineSegment(sketch, "E120", {"start": v(16.5, 72.25) * mm, "end": v(13.6, 72.25) * mm});
            skLineSegment(sketch, "E121", {"start": v(13.6, 76.75) * mm, "end": v(13.6, 72.25) * mm});
            const initialGuessF10  = {"E111.0.2": [0, 0.07367181871006903, -1, 0, 0.009, 0.0030781812899310194, 4.71238898038469, 0]};
            skSetInitialGuess(sketch, initialGuessF10);
            skSolve(sketch);
        }
        {
            var Q0;
            {var subQ8=sQuery(id+"F10.wireOp",EDGE,"E113");var subQ9=sQuery(id+"F10.wireOp",EDGE,"E112");var subQ10=makeQuery(id+"F10.imprint","INTERSECT",VERTEX,{"derivedFrom":[subQ9,subQ8]});Q0=makeQuery(id+"F10.imprint","IMPRINT",FACE,{"disambiguationData":[TD([[makeQuery(id+"F10.imprint","IMPRINT",EDGE,{"disambiguationData":[TD([[subQ10,1.0]])],"derivedFrom":subQ9}),1.0]])]});}
            var Q1;
            {var subQ0=sQuery(id+"F10.wireOp",EDGE,"E121");var subQ1=sQuery(id+"F10.wireOp",EDGE,"E114");var subQ2=makeQuery(id+"F10.imprint","INTERSECT",VERTEX,{"derivedFrom":[subQ1,subQ0]});Q1=makeQuery(id+"F10.imprint","IMPRINT",FACE,{"disambiguationData":[TD([[makeQuery(id+"F10.imprint","IMPRINT",EDGE,{"disambiguationData":[TD([[subQ2,-1.0]])],"derivedFrom":subQ1}),-1.0]])]});}
            var Q2;
            {var subQ0=sQuery(id+"F10.wireOp",EDGE,"E119");var subQ1=sQuery(id+"F10.wireOp",EDGE,"E118");var subQ2=makeQuery(id+"F10.imprint","INTERSECT",VERTEX,{"derivedFrom":[subQ1,subQ0]});Q2=makeQuery(id+"F10.imprint","IMPRINT",FACE,{"disambiguationData":[TD([[makeQuery(id+"F10.imprint","IMPRINT",EDGE,{"disambiguationData":[TD([[subQ2,1.0]])],"derivedFrom":subQ1}),1.0]])]});}
            var Q3;
            {var subQ5=sQuery(id+"F10.wireOp",EDGE,"E116");var subQ9=sQuery(id+"F10.wireOp",EDGE,"E115");var subQ10=makeQuery(id+"F10.imprint","INTERSECT",VERTEX,{"derivedFrom":[subQ9,subQ5]});Q3=makeQuery(id+"F10.imprint","IMPRINT",FACE,{"disambiguationData":[TD([[makeQuery(id+"F10.imprint","IMPRINT",EDGE,{"disambiguationData":[TD([[subQ10,1.0]])],"derivedFrom":subQ9}),-1.0]])]});}
            var Q4;
            {var subQ0=sQuery(id+"F10.wireOp",EDGE,"E119");var subQ1=sQuery(id+"F10.wireOp",EDGE,"E116");var subQ2=makeQuery(id+"F10.imprint","INTERSECT",VERTEX,{"derivedFrom":[subQ1,subQ0]});Q4=makeQuery(id+"F10.imprint","IMPRINT",FACE,{"disambiguationData":[TD([[makeQuery(id+"F10.imprint","IMPRINT",EDGE,{"disambiguationData":[TD([[subQ2,-1.0]])],"derivedFrom":subQ1}),1.0]])]});}
            var Q5;
            {var subQ0=sQuery(id+"F10.wireOp",EDGE,"E114");var subQ1=sQuery(id+"F10.wireOp",EDGE,"E113");var subQ2=makeQuery(id+"F10.imprint","INTERSECT",VERTEX,{"derivedFrom":[subQ1,subQ0]});Q5=makeQuery(id+"F10.imprint","IMPRINT",FACE,{"disambiguationData":[TD([[makeQuery(id+"F10.imprint","IMPRINT",EDGE,{"disambiguationData":[TD([[subQ2,-1.0]])],"derivedFrom":subQ1}),-1.0]])]});}
            extrude(context, id + "F11", {"entities" : qUnion([Q0, Q1, Q2, Q3, Q4, Q5]), "operationType" : NewBodyOperationType.REMOVE, "depth" : 50 * mm});
        }
        {
            var Q0;
            Q0=makeQuery(id+"F6.imprint","IMPRINT",FACE,{"disambiguationData":[TD([[makeQuery(id+"F6.imprint","IMPRINT",EDGE,{"derivedFrom":sQuery(id+"F6.wireOp",EDGE,"E90")}),1.0]])]});
            var Q1;
            Q1=makeQuery(id+"F6.imprint","IMPRINT",FACE,{"disambiguationData":[TD([[makeQuery(id+"F6.imprint","IMPRINT",EDGE,{"derivedFrom":sQuery(id+"F6.wireOp",EDGE,"E91")}),1.0]])]});
            var Q2;
            Q2=makeQuery(id+"F6.imprint","IMPRINT",FACE,{"disambiguationData":[TD([[makeQuery(id+"F6.imprint","IMPRINT",EDGE,{"derivedFrom":sQuery(id+"F6.wireOp",EDGE,"E93")}),1.0]])]});
            var Q3;
            Q3=makeQuery(id+"F6.imprint","IMPRINT",FACE,{"disambiguationData":[TD([[makeQuery(id+"F6.imprint","IMPRINT",EDGE,{"derivedFrom":sQuery(id+"F6.wireOp",EDGE,"E92")}),1.0]])]});
            extrude(context, id + "F12", {"entities" : qUnion([Q0, Q1, Q2, Q3]), "operationType" : NewBodyOperationType.REMOVE, "oppositeDirection" : true, "depth" : 1.25 * mm});
        }
    });
